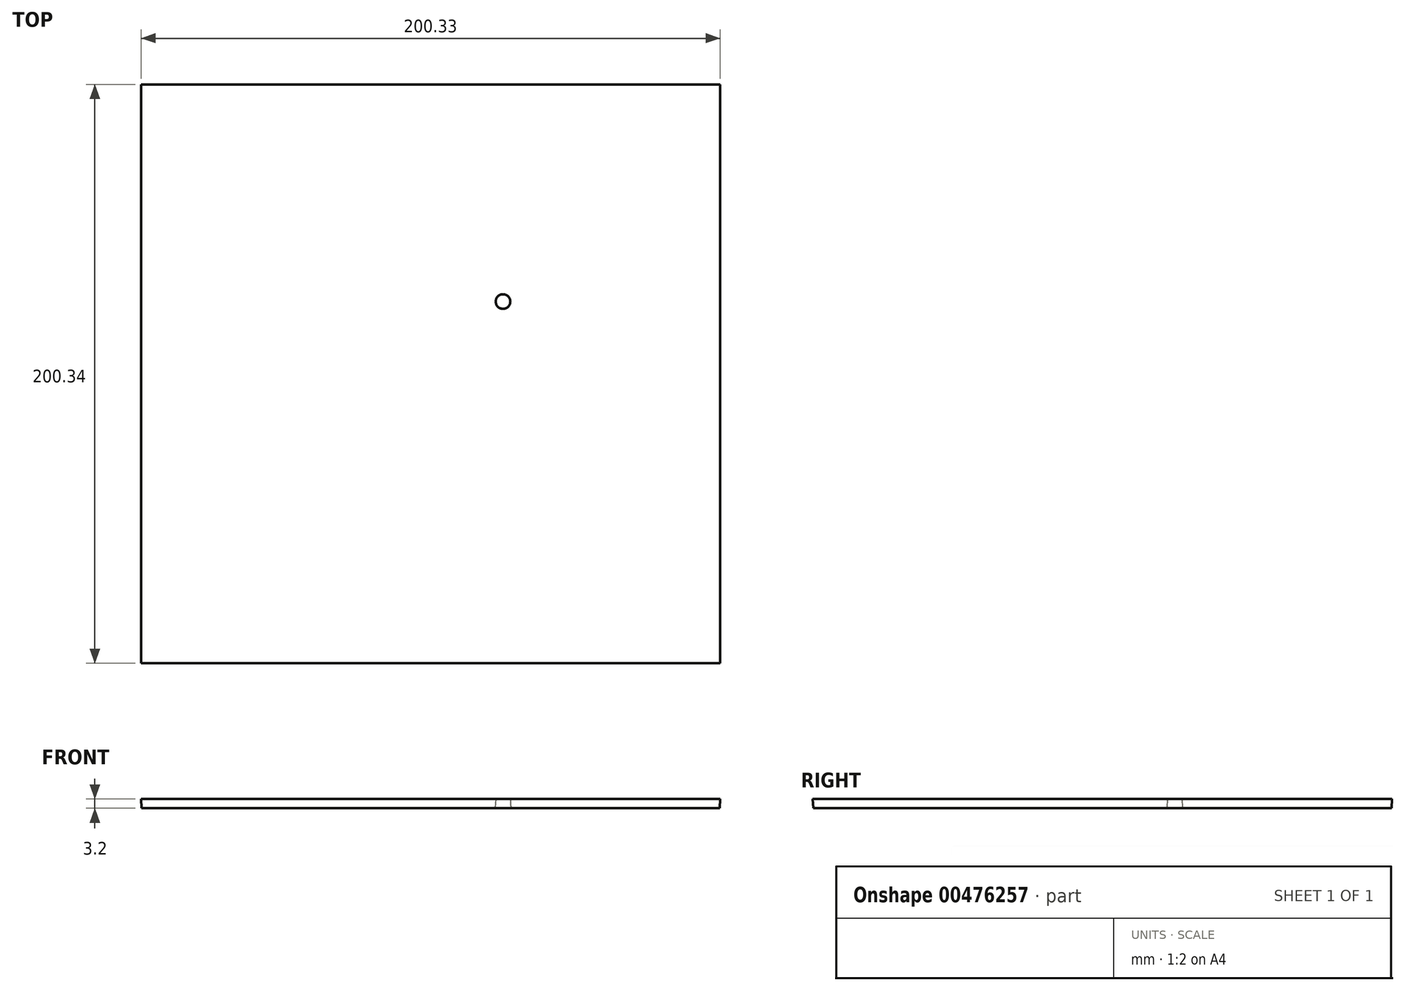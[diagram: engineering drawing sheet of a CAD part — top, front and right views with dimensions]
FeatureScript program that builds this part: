
annotation { "Feature Type Name" : "Feature", "Feature Type Description" : "" }
export const myFeature = defineFeature(function(context is Context, id is Id, definition is map)
    precondition{}
    {
        {
            var Q0;
            Q0=qCreatedBy(makeId("Top.planeOp"),FACE);
            var sketch = newSketch(context, id + "F0", { "sketchPlane" : qUnion([Q0])});
            skLineSegment(sketch, "E0.bottom", {"start": v(-92.42, 120.73) * mm, "end": v(107.58, 120.73) * mm});
            skLineSegment(sketch, "E0.top", {"start": v(-92.42, -79.27) * mm, "end": v(107.58, -79.27) * mm});
            skLineSegment(sketch, "E0.left", {"start": v(-92.42, 120.73) * mm, "end": v(-92.42, -79.27) * mm});
            skLineSegment(sketch, "E0.right", {"start": v(107.58, 120.73) * mm, "end": v(107.58, -79.27) * mm});
            skCircle(sketch, "E1", {"center": v(32.58, 45.73) * mm, "radius": 2.7 * mm});
            skSolve(sketch);
        }
        {
            var Q0;
            Q0 = qSketchRegion(id + "F0", true);
            extrude(context, id + "F1", {"entities" : qUnion([Q0]), "depth" : 3.2 * mm, "hasDraft" : true, "draftAngle" : 3 * degree});
        }
    });
